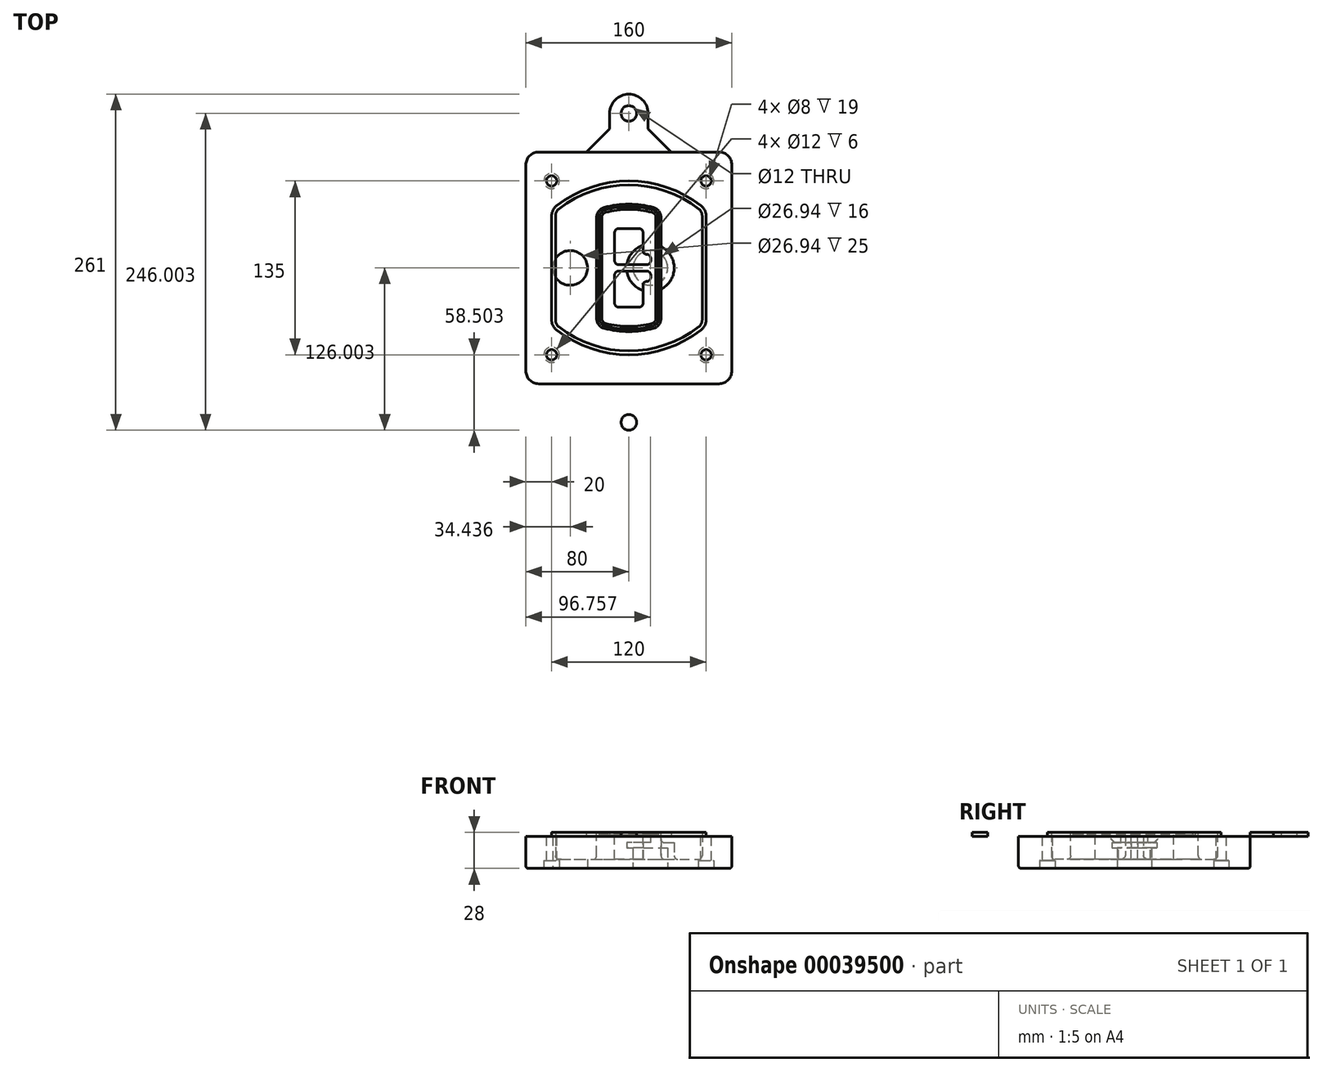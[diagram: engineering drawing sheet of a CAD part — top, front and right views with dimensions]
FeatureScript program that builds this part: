
annotation { "Feature Type Name" : "Feature", "Feature Type Description" : "" }
export const myFeature = defineFeature(function(context is Context, id is Id, definition is map)
    precondition{}
    {
        {
            var Q0;
            Q0=qCreatedBy(makeId("Top.planeOp"),FACE);
            var sketch = newSketch(context, id + "F0", { "sketchPlane" : qUnion([Q0])});
            skPoint(sketch, "E0.rect.middle", {"position": v(0, 0) * mm});
            skLineSegment(sketch, "E1.bottom", {"start": v(24.05, 28.38) * mm, "end": v(164.05, 28.38) * mm});
            skLineSegment(sketch, "E1.top", {"start": v(24.05, 208.38) * mm, "end": v(164.05, 208.38) * mm});
            skLineSegment(sketch, "E1.left", {"start": v(14.05, 38.38) * mm, "end": v(14.05, 198.38) * mm});
            skLineSegment(sketch, "E1.right", {"start": v(174.05, 38.38) * mm, "end": v(174.05, 198.38) * mm});
            skLineSegment(sketch, "E2", {"start": v(14.05, 208.38) * mm, "end": v(174.05, 28.38) * mm, "construction": true});
            skLineSegment(sketch, "E3", {"start": v(174.05, 208.38) * mm, "end": v(14.05, 28.38) * mm, "construction": true});
            skCircle(sketch, "E4", {"center": v(34.05, 185.88) * mm, "radius": 4 * mm});
            skCircle(sketch, "E5", {"center": v(154.05, 185.88) * mm, "radius": 4 * mm});
            skCircle(sketch, "E6", {"center": v(154.05, 50.88) * mm, "radius": 4 * mm});
            skCircle(sketch, "E7", {"center": v(34.05, 50.88) * mm, "radius": 4 * mm});
            skLineSegment(sketch, "E8", {"start": v(34.05, 185.88) * mm, "end": v(154.05, 185.88) * mm, "construction": true});
            skLineSegment(sketch, "E9", {"start": v(154.05, 185.88) * mm, "end": v(154.05, 50.88) * mm, "construction": true});
            skLineSegment(sketch, "E10", {"start": v(154.05, 50.88) * mm, "end": v(34.05, 50.88) * mm, "construction": true});
            skLineSegment(sketch, "E11", {"start": v(34.05, 50.88) * mm, "end": v(34.05, 185.88) * mm, "construction": true});
            skLineSegment(sketch, "E12", {"start": v(34.05, 158.68) * mm, "end": v(34.05, 78.09) * mm});
            skLineSegment(sketch, "E13", {"start": v(154.05, 158.68) * mm, "end": v(154.05, 78.09) * mm});
            skArc(sketch, "E14", {"start": v(150.2, 166.56) * mm, "mid": v(94.05, 185.88) * mm, "end": v(37.9, 166.56) * mm});
            skArc(sketch, "E15", {"start": v(37.9, 70.2) * mm, "mid": v(94.05, 50.88) * mm, "end": v(150.2, 70.2) * mm});
            skLineSegment(sketch, "E16", {"start": v(34.05, 118.38) * mm, "end": v(154.05, 118.38) * mm, "construction": true});
            skPoint(sketch, "E17.visualSharp", {"position": v(34.05, 73.38) * mm});
            skArc(sketch, "E17.filletArc", {"start": v(34.05, 78.09) * mm, "mid": v(35.06, 73.7) * mm, "end": v(37.9, 70.2) * mm});
            skPoint(sketch, "E18.visualSharp", {"position": v(34.05, 163.38) * mm});
            skArc(sketch, "E18.filletArc", {"start": v(37.9, 166.56) * mm, "mid": v(35.06, 163.06) * mm, "end": v(34.05, 158.68) * mm});
            skPoint(sketch, "E19.visualSharp", {"position": v(154.05, 163.38) * mm});
            skArc(sketch, "E19.filletArc", {"start": v(154.05, 158.68) * mm, "mid": v(153.04, 163.06) * mm, "end": v(150.2, 166.56) * mm});
            skPoint(sketch, "E20.visualSharp", {"position": v(154.05, 73.38) * mm});
            skArc(sketch, "E20.filletArc", {"start": v(150.2, 70.2) * mm, "mid": v(153.04, 73.7) * mm, "end": v(154.05, 78.09) * mm});
            skPoint(sketch, "E21.visualSharp", {"position": v(14.05, 208.38) * mm});
            skArc(sketch, "E21.filletArc", {"start": v(24.05, 208.38) * mm, "mid": v(16.98, 205.45) * mm, "end": v(14.05, 198.38) * mm});
            skPoint(sketch, "E22.visualSharp", {"position": v(174.05, 208.38) * mm});
            skArc(sketch, "E22.filletArc", {"start": v(174.05, 198.38) * mm, "mid": v(171.12, 205.45) * mm, "end": v(164.05, 208.38) * mm});
            skPoint(sketch, "E23.visualSharp", {"position": v(174.05, 28.38) * mm});
            skArc(sketch, "E23.filletArc", {"start": v(164.05, 28.38) * mm, "mid": v(171.12, 31.31) * mm, "end": v(174.05, 38.38) * mm});
            skPoint(sketch, "E24.visualSharp", {"position": v(14.05, 28.38) * mm});
            skArc(sketch, "E24.filletArc", {"start": v(14.05, 38.38) * mm, "mid": v(16.98, 31.31) * mm, "end": v(24.05, 28.38) * mm});
            skArc(sketch, "E25.0", {"start": v(151.05, 158.68) * mm, "mid": v(150.34, 161.75) * mm, "end": v(148.36, 164.2) * mm});
            skLineSegment(sketch, "E25.1", {"start": v(151.05, 158.68) * mm, "end": v(151.05, 78.09) * mm});
            skArc(sketch, "E25.2", {"start": v(148.36, 72.57) * mm, "mid": v(150.34, 75.02) * mm, "end": v(151.05, 78.09) * mm});
            skArc(sketch, "E25.3", {"start": v(39.74, 72.57) * mm, "mid": v(94.05, 53.88) * mm, "end": v(148.36, 72.57) * mm});
            skArc(sketch, "E25.4", {"start": v(37.05, 78.09) * mm, "mid": v(37.76, 75.02) * mm, "end": v(39.74, 72.57) * mm});
            skArc(sketch, "E25.5", {"start": v(148.36, 164.2) * mm, "mid": v(94.05, 182.88) * mm, "end": v(39.74, 164.2) * mm});
            skLineSegment(sketch, "E25.6", {"start": v(37.05, 158.68) * mm, "end": v(37.05, 78.09) * mm});
            skArc(sketch, "E25.7", {"start": v(39.74, 164.2) * mm, "mid": v(37.76, 161.75) * mm, "end": v(37.05, 158.68) * mm});
            skArc(sketch, "E26.0", {"start": v(35.43, 169.71) * mm, "mid": v(31.47, 164.82) * mm, "end": v(30.05, 158.68) * mm});
            skArc(sketch, "E26.1", {"start": v(152.67, 169.71) * mm, "mid": v(94.05, 189.88) * mm, "end": v(35.43, 169.71) * mm});
            skArc(sketch, "E26.2", {"start": v(158.05, 158.68) * mm, "mid": v(156.63, 164.82) * mm, "end": v(152.67, 169.71) * mm});
            skLineSegment(sketch, "E26.3", {"start": v(158.05, 158.68) * mm, "end": v(158.05, 78.09) * mm});
            skArc(sketch, "E26.4", {"start": v(152.67, 67.05) * mm, "mid": v(156.63, 71.95) * mm, "end": v(158.05, 78.09) * mm});
            skLineSegment(sketch, "E26.5", {"start": v(30.05, 158.68) * mm, "end": v(30.05, 78.09) * mm});
            skArc(sketch, "E26.6", {"start": v(35.43, 67.05) * mm, "mid": v(94.05, 46.88) * mm, "end": v(152.67, 67.05) * mm});
            skArc(sketch, "E26.7", {"start": v(30.05, 78.09) * mm, "mid": v(31.47, 71.95) * mm, "end": v(35.43, 67.05) * mm});
            skSolve(sketch);
        }
        {
            var Q0;
            Q0=makeQuery(id+"F0.imprint","IMPRINT",FACE,{"disambiguationData":[TD([[makeQuery(id+"F0.imprint","IMPRINT",EDGE,{"derivedFrom":sQuery(id+"F0.wireOp",EDGE,"E1.bottom")}),1.0]])]});
            var Q1;
            Q1=makeQuery(id+"F0.imprint","IMPRINT",FACE,{"disambiguationData":[TD([[makeQuery(id+"F0.imprint","IMPRINT",EDGE,{"derivedFrom":sQuery(id+"F0.wireOp",EDGE,"E12")}),1.0]])]});
            var Q2;
            Q2=makeQuery(id+"F0.imprint","IMPRINT",FACE,{"disambiguationData":[TD([[makeQuery(id+"F0.imprint","IMPRINT",EDGE,{"derivedFrom":sQuery(id+"F0.wireOp",EDGE,"E25.0")}),1.0]])]});
            var Q3;
            Q3=makeQuery(id+"F0.imprint","IMPRINT",FACE,{"disambiguationData":[TD([[makeQuery(id+"F0.imprint","IMPRINT",EDGE,{"derivedFrom":sQuery(id+"F0.wireOp",EDGE,"E12")}),-1.0]])]});
            extrude(context, id + "F1", {"entities" : qUnion([Q0, Q1, Q2, Q3]), "oppositeDirection" : true, "depth" : 25 * mm});
        }
        {
            var Q0;
            Q0=makeQuery(id+"F0.imprint","IMPRINT",FACE,{"disambiguationData":[TD([[makeQuery(id+"F0.imprint","IMPRINT",EDGE,{"derivedFrom":sQuery(id+"F0.wireOp",EDGE,"E12")}),1.0]])]});
            extrude(context, id + "F2", {"entities" : qUnion([Q0]), "operationType" : NewBodyOperationType.ADD, "depth" : 3 * mm});
        }
        {
            var Q0;
            Q0=makeQuery(id+"F0.imprint","IMPRINT",FACE,{"disambiguationData":[TD([[makeQuery(id+"F0.imprint","IMPRINT",EDGE,{"derivedFrom":sQuery(id+"F0.wireOp",EDGE,"E25.0")}),1.0]])]});
            extrude(context, id + "F3", {"entities" : qUnion([Q0]), "operationType" : NewBodyOperationType.REMOVE, "oppositeDirection" : true, "depth" : 18 * mm});
        }
        {
            var Q0;
            Q0=makeQuery(id+"F2.opExtrude","CAP_FACE",FACE,{"disambiguationData":[OSD([sQuery(id+"F0.wireOp",EDGE,"E12"),sQuery(id+"F0.wireOp",EDGE,"E13"),sQuery(id+"F0.wireOp",EDGE,"E14"),sQuery(id+"F0.wireOp",EDGE,"E15"),sQuery(id+"F0.wireOp",EDGE,"E17.filletArc"),sQuery(id+"F0.wireOp",EDGE,"E18.filletArc"),sQuery(id+"F0.wireOp",EDGE,"E19.filletArc"),sQuery(id+"F0.wireOp",EDGE,"E20.filletArc"),sQuery(id+"F0.wireOp",EDGE,"E25.0"),sQuery(id+"F0.wireOp",EDGE,"E25.1"),sQuery(id+"F0.wireOp",EDGE,"E25.2"),sQuery(id+"F0.wireOp",EDGE,"E25.3"),sQuery(id+"F0.wireOp",EDGE,"E25.4"),sQuery(id+"F0.wireOp",EDGE,"E25.5"),sQuery(id+"F0.wireOp",EDGE,"E25.6"),sQuery(id+"F0.wireOp",EDGE,"E25.7")])],"isStart":false});
            var sketch = newSketch(context, id + "F4", { "sketchPlane" : qUnion([Q0])});
            skArc(sketch, "E27.0", {"start": v(74.97, 71.41) * mm, "mid": v(94.05, 68.88) * mm, "end": v(113.13, 71.41) * mm});
            skArc(sketch, "E28.0", {"start": v(113.13, 165.35) * mm, "mid": v(94.05, 167.88) * mm, "end": v(74.97, 165.35) * mm});
            skLineSegment(sketch, "E29", {"start": v(69.05, 157.63) * mm, "end": v(69.05, 79.14) * mm});
            skLineSegment(sketch, "E30", {"start": v(119.05, 157.63) * mm, "end": v(119.05, 79.14) * mm});
            skLineSegment(sketch, "E31", {"start": v(69.05, 163.48) * mm, "end": v(119.05, 163.48) * mm, "construction": true});
            skLineSegment(sketch, "E32", {"start": v(69.05, 73.28) * mm, "end": v(119.05, 73.28) * mm, "construction": true});
            skPoint(sketch, "E33.visualSharp", {"position": v(69.05, 163.48) * mm});
            skArc(sketch, "E33.filletArc", {"start": v(74.97, 165.35) * mm, "mid": v(70.7, 162.5) * mm, "end": v(69.05, 157.63) * mm});
            skPoint(sketch, "E34.visualSharp", {"position": v(119.05, 163.48) * mm});
            skArc(sketch, "E34.filletArc", {"start": v(119.05, 157.63) * mm, "mid": v(117.4, 162.5) * mm, "end": v(113.13, 165.35) * mm});
            skPoint(sketch, "E35.visualSharp", {"position": v(119.05, 73.28) * mm});
            skArc(sketch, "E35.filletArc", {"start": v(113.13, 71.41) * mm, "mid": v(117.4, 74.27) * mm, "end": v(119.05, 79.14) * mm});
            skPoint(sketch, "E36.visualSharp", {"position": v(69.05, 73.28) * mm});
            skArc(sketch, "E36.filletArc", {"start": v(69.05, 79.14) * mm, "mid": v(70.7, 74.27) * mm, "end": v(74.97, 71.41) * mm});
            skArc(sketch, "E37.0", {"start": v(148.36, 164.2) * mm, "mid": v(94.05, 182.88) * mm, "end": v(39.74, 164.2) * mm});
            skArc(sketch, "E37.1", {"start": v(39.74, 164.2) * mm, "mid": v(37.76, 161.75) * mm, "end": v(37.05, 158.68) * mm});
            skLineSegment(sketch, "E37.2", {"start": v(37.05, 158.68) * mm, "end": v(37.05, 78.09) * mm});
            skArc(sketch, "E37.3", {"start": v(37.05, 78.09) * mm, "mid": v(37.76, 75.02) * mm, "end": v(39.74, 72.57) * mm});
            skArc(sketch, "E37.4", {"start": v(39.74, 72.57) * mm, "mid": v(94.05, 53.88) * mm, "end": v(148.36, 72.57) * mm});
            skArc(sketch, "E37.5", {"start": v(148.36, 72.57) * mm, "mid": v(150.34, 75.02) * mm, "end": v(151.05, 78.09) * mm});
            skLineSegment(sketch, "E37.6", {"start": v(151.05, 158.68) * mm, "end": v(151.05, 78.09) * mm});
            skArc(sketch, "E37.7", {"start": v(151.05, 158.68) * mm, "mid": v(150.34, 161.75) * mm, "end": v(148.36, 164.2) * mm});
            skLineSegment(sketch, "E38.0", {"start": v(117.05, 157.63) * mm, "end": v(117.05, 79.14) * mm});
            skArc(sketch, "E38.1", {"start": v(112.61, 73.34) * mm, "mid": v(115.81, 75.49) * mm, "end": v(117.05, 79.14) * mm});
            skArc(sketch, "E38.2", {"start": v(75.49, 73.34) * mm, "mid": v(94.05, 70.88) * mm, "end": v(112.61, 73.34) * mm});
            skArc(sketch, "E38.3", {"start": v(71.05, 79.14) * mm, "mid": v(72.29, 75.49) * mm, "end": v(75.49, 73.34) * mm});
            skLineSegment(sketch, "E38.4", {"start": v(71.05, 157.63) * mm, "end": v(71.05, 79.14) * mm});
            skArc(sketch, "E38.5", {"start": v(117.05, 157.63) * mm, "mid": v(115.81, 161.28) * mm, "end": v(112.61, 163.42) * mm});
            skArc(sketch, "E38.6", {"start": v(75.49, 163.42) * mm, "mid": v(72.29, 161.28) * mm, "end": v(71.05, 157.63) * mm});
            skArc(sketch, "E38.7", {"start": v(112.61, 163.42) * mm, "mid": v(94.05, 165.88) * mm, "end": v(75.49, 163.42) * mm});
            skArc(sketch, "E39.0", {"start": v(115.05, 157.63) * mm, "mid": v(114.23, 160.06) * mm, "end": v(112.1, 161.5) * mm});
            skLineSegment(sketch, "E39.1", {"start": v(115.05, 157.63) * mm, "end": v(115.05, 79.14) * mm});
            skArc(sketch, "E39.2", {"start": v(112.1, 75.27) * mm, "mid": v(114.23, 76.7) * mm, "end": v(115.05, 79.14) * mm});
            skArc(sketch, "E39.3", {"start": v(76, 75.27) * mm, "mid": v(94.05, 72.88) * mm, "end": v(112.1, 75.27) * mm});
            skArc(sketch, "E39.4", {"start": v(73.05, 79.14) * mm, "mid": v(73.87, 76.7) * mm, "end": v(76, 75.27) * mm});
            skArc(sketch, "E39.5", {"start": v(112.1, 161.5) * mm, "mid": v(94.05, 163.88) * mm, "end": v(76, 161.5) * mm});
            skLineSegment(sketch, "E39.6", {"start": v(73.05, 157.63) * mm, "end": v(73.05, 79.14) * mm});
            skArc(sketch, "E39.7", {"start": v(76, 161.5) * mm, "mid": v(73.87, 160.06) * mm, "end": v(73.05, 157.63) * mm});
            skLineSegment(sketch, "E40", {"start": v(69.05, 118.38) * mm, "end": v(119.05, 118.38) * mm, "construction": true});
            skLineSegment(sketch, "E41", {"start": v(83.05, 123.88) * mm, "end": v(83.05, 145.88) * mm});
            skLineSegment(sketch, "E42", {"start": v(86.05, 148.88) * mm, "end": v(102.05, 148.88) * mm});
            skLineSegment(sketch, "E43", {"start": v(105.05, 145.88) * mm, "end": v(105.05, 131.88) * mm});
            skLineSegment(sketch, "E44", {"start": v(108.05, 128.88) * mm, "end": v(108.05, 128.88) * mm});
            skLineSegment(sketch, "E45", {"start": v(111.05, 125.88) * mm, "end": v(111.05, 123.88) * mm});
            skLineSegment(sketch, "E46", {"start": v(108.05, 120.88) * mm, "end": v(86.05, 120.88) * mm});
            skPoint(sketch, "E47.visualSharp", {"position": v(83.05, 148.88) * mm});
            skArc(sketch, "E47.filletArc", {"start": v(86.05, 148.88) * mm, "mid": v(83.93, 148) * mm, "end": v(83.05, 145.88) * mm});
            skPoint(sketch, "E48.visualSharp", {"position": v(105.05, 148.88) * mm});
            skArc(sketch, "E48.filletArc", {"start": v(105.05, 145.88) * mm, "mid": v(104.17, 148) * mm, "end": v(102.05, 148.88) * mm});
            skPoint(sketch, "E49.visualSharp", {"position": v(105.05, 128.88) * mm});
            skArc(sketch, "E49.filletArc", {"start": v(105.05, 131.88) * mm, "mid": v(105.93, 129.76) * mm, "end": v(108.05, 128.88) * mm});
            skPoint(sketch, "E50.visualSharp", {"position": v(111.05, 128.88) * mm});
            skArc(sketch, "E50.filletArc", {"start": v(111.05, 125.88) * mm, "mid": v(110.17, 128) * mm, "end": v(108.05, 128.88) * mm});
            skPoint(sketch, "E51.visualSharp", {"position": v(111.05, 120.88) * mm});
            skArc(sketch, "E51.filletArc", {"start": v(108.05, 120.88) * mm, "mid": v(110.17, 121.76) * mm, "end": v(111.05, 123.88) * mm});
            skPoint(sketch, "E52.visualSharp", {"position": v(83.05, 120.88) * mm});
            skArc(sketch, "E52.filletArc", {"start": v(83.05, 123.88) * mm, "mid": v(83.93, 121.76) * mm, "end": v(86.05, 120.88) * mm});
            skLineSegment(sketch, "E53.0.MirrorCS", {"start": v(108.05, 115.88) * mm, "end": v(86.05, 115.88) * mm});
            skArc(sketch, "E54.0.MirrorCS", {"start": v(83.05, 112.88) * mm, "mid": v(83.93, 115) * mm, "end": v(86.05, 115.88) * mm});
            skLineSegment(sketch, "E55.0.MirrorCS", {"start": v(83.05, 112.88) * mm, "end": v(83.05, 90.88) * mm});
            skArc(sketch, "E56.0.MirrorCS", {"start": v(86.05, 87.88) * mm, "mid": v(83.93, 88.76) * mm, "end": v(83.05, 90.88) * mm});
            skLineSegment(sketch, "E57.0.MirrorCS", {"start": v(86.05, 87.88) * mm, "end": v(102.05, 87.88) * mm});
            skArc(sketch, "E58.0.MirrorCS", {"start": v(105.05, 90.88) * mm, "mid": v(104.17, 88.76) * mm, "end": v(102.05, 87.88) * mm});
            skLineSegment(sketch, "E59.0.MirrorCS", {"start": v(105.05, 90.88) * mm, "end": v(105.05, 104.88) * mm});
            skArc(sketch, "E60.0.MirrorCS", {"start": v(105.05, 104.88) * mm, "mid": v(105.93, 107) * mm, "end": v(108.05, 107.88) * mm});
            skArc(sketch, "E61.0.MirrorCS", {"start": v(111.05, 110.88) * mm, "mid": v(110.17, 108.76) * mm, "end": v(108.05, 107.88) * mm});
            skLineSegment(sketch, "E62.0.MirrorCS", {"start": v(111.05, 110.88) * mm, "end": v(111.05, 112.88) * mm});
            skArc(sketch, "E63.0.MirrorCS", {"start": v(108.05, 115.88) * mm, "mid": v(110.17, 115) * mm, "end": v(111.05, 112.88) * mm});
            skSolve(sketch);
        }
        {
            var Q0;
            Q0=makeQuery(id+"F4.imprint","IMPRINT",FACE,{"disambiguationData":[TD([[makeQuery(id+"F4.imprint","IMPRINT",EDGE,{"derivedFrom":sQuery(id+"F4.wireOp",EDGE,"E27.0")}),1.0]])]});
            var Q1;
            Q1=makeQuery(id+"F4.imprint","IMPRINT",FACE,{"disambiguationData":[TD([[makeQuery(id+"F4.imprint","IMPRINT",EDGE,{"derivedFrom":sQuery(id+"F4.wireOp",EDGE,"E38.0")}),-1.0]])]});
            var Q2;
            Q2=makeQuery(id+"F4.imprint","IMPRINT",FACE,{"disambiguationData":[TD([[makeQuery(id+"F4.imprint","IMPRINT",EDGE,{"derivedFrom":sQuery(id+"F4.wireOp",EDGE,"E39.0")}),1.0]])]});
            extrude(context, id + "F5", {"entities" : qUnion([Q0, Q1, Q2]), "operationType" : NewBodyOperationType.ADD, "endBound" : BoundingType.UP_TO_NEXT, "oppositeDirection" : true, "depth" : 25 * mm});
        }
        {
            var Q0;
            Q0=makeQuery(id+"F4.imprint","IMPRINT",FACE,{"disambiguationData":[TD([[makeQuery(id+"F4.imprint","IMPRINT",EDGE,{"derivedFrom":sQuery(id+"F4.wireOp",EDGE,"E38.0")}),-1.0]])]});
            extrude(context, id + "F6", {"entities" : qUnion([Q0]), "operationType" : NewBodyOperationType.REMOVE, "oppositeDirection" : true, "depth" : 2 * mm});
        }
        {
            var Q0;
            Q0=makeQuery(id+"F1.opExtrude","CAP_FACE",FACE,{"disambiguationData":[OSD([sQuery(id+"F0.wireOp",EDGE,"E1.bottom"),sQuery(id+"F0.wireOp",EDGE,"E1.top"),sQuery(id+"F0.wireOp",EDGE,"E1.left"),sQuery(id+"F0.wireOp",EDGE,"E1.right"),sQuery(id+"F0.wireOp",EDGE,"E4"),sQuery(id+"F0.wireOp",EDGE,"E5"),sQuery(id+"F0.wireOp",EDGE,"E6"),sQuery(id+"F0.wireOp",EDGE,"E7"),sQuery(id+"F0.wireOp",EDGE,"E21.filletArc"),sQuery(id+"F0.wireOp",EDGE,"E22.filletArc"),sQuery(id+"F0.wireOp",EDGE,"E23.filletArc"),sQuery(id+"F0.wireOp",EDGE,"E24.filletArc")])],"isStart":false});
            var sketch = newSketch(context, id + "F7", { "sketchPlane" : qUnion([Q0])});
            skCircle(sketch, "E64", {"center": v(110.8, -118.38) * mm, "radius": 13.47 * mm});
            skCircle(sketch, "E65", {"center": v(48.49, -118.38) * mm, "radius": 13.47 * mm});
            skLineSegment(sketch, "E66", {"start": v(174.05, -118.38) * mm, "end": v(14.05, -118.38) * mm});
            skCircle(sketch, "E67", {"center": v(110.8, -118.38) * mm, "radius": 18.47 * mm});
            skCircle(sketch, "E68", {"center": v(154.05, -185.88) * mm, "radius": 6 * mm});
            skCircle(sketch, "E69", {"center": v(34.05, -185.88) * mm, "radius": 6 * mm});
            skCircle(sketch, "E70", {"center": v(34.05, -50.88) * mm, "radius": 6 * mm});
            skCircle(sketch, "E71", {"center": v(154.05, -50.88) * mm, "radius": 6 * mm});
            skSolve(sketch);
        }
        {
            var Q0;
            {var subQ1=sQuery(id+"F7.wireOp",EDGE,"E66");var subQ4=sQuery(id+"F7.wireOp",EDGE,"E64");var subQ6=makeQuery(id+"F7.imprint","INTERSECT",VERTEX,{"disambiguationData":[OD(0.0)],"derivedFrom":[subQ4,subQ1]});Q0=makeQuery(id+"F7.imprint","IMPRINT",FACE,{"disambiguationData":[TD([[makeQuery(id+"F7.imprint","IMPRINT",EDGE,{"disambiguationData":[TD([[subQ6,-1.0]])],"derivedFrom":subQ4}),-1.0]])]});}
            var Q1;
            {var subQ0=sQuery(id+"F7.wireOp",EDGE,"E66");var subQ1=sQuery(id+"F7.wireOp",EDGE,"E64");var subQ3=makeQuery(id+"F7.imprint","INTERSECT",VERTEX,{"disambiguationData":[OD(0.0)],"derivedFrom":[subQ1,subQ0]});Q1=makeQuery(id+"F7.imprint","IMPRINT",FACE,{"disambiguationData":[TD([[makeQuery(id+"F7.imprint","IMPRINT",EDGE,{"disambiguationData":[TD([[subQ3,-1.0]])],"derivedFrom":subQ1}),1.0]])]});}
            var Q2;
            {var subQ0=sQuery(id+"F7.wireOp",EDGE,"E66");var subQ1=sQuery(id+"F7.wireOp",EDGE,"E64");var subQ3=makeQuery(id+"F7.imprint","INTERSECT",VERTEX,{"disambiguationData":[OD(0.0)],"derivedFrom":[subQ1,subQ0]});Q2=makeQuery(id+"F7.imprint","IMPRINT",FACE,{"disambiguationData":[TD([[makeQuery(id+"F7.imprint","IMPRINT",EDGE,{"disambiguationData":[TD([[subQ3,1.0]])],"derivedFrom":subQ1}),1.0]])]});}
            var Q3;
            {var subQ1=sQuery(id+"F7.wireOp",EDGE,"E66");var subQ4=sQuery(id+"F7.wireOp",EDGE,"E64");var subQ6=makeQuery(id+"F7.imprint","INTERSECT",VERTEX,{"disambiguationData":[OD(0.0)],"derivedFrom":[subQ4,subQ1]});Q3=makeQuery(id+"F7.imprint","IMPRINT",FACE,{"disambiguationData":[TD([[makeQuery(id+"F7.imprint","IMPRINT",EDGE,{"disambiguationData":[TD([[subQ6,1.0]])],"derivedFrom":subQ4}),-1.0]])]});}
            extrude(context, id + "F8", {"entities" : qUnion([Q0, Q1, Q2, Q3]), "operationType" : NewBodyOperationType.ADD, "oppositeDirection" : true, "depth" : 20 * mm});
        }
        {
            var Q0;
            {var subQ0=sQuery(id+"F7.wireOp",EDGE,"E66");var subQ1=sQuery(id+"F7.wireOp",EDGE,"E64");var subQ3=makeQuery(id+"F7.imprint","INTERSECT",VERTEX,{"disambiguationData":[OD(0.0)],"derivedFrom":[subQ1,subQ0]});Q0=makeQuery(id+"F7.imprint","IMPRINT",FACE,{"disambiguationData":[TD([[makeQuery(id+"F7.imprint","IMPRINT",EDGE,{"disambiguationData":[TD([[subQ3,-1.0]])],"derivedFrom":subQ1}),1.0]])]});}
            var Q1;
            {var subQ0=sQuery(id+"F7.wireOp",EDGE,"E66");var subQ1=sQuery(id+"F7.wireOp",EDGE,"E64");var subQ3=makeQuery(id+"F7.imprint","INTERSECT",VERTEX,{"disambiguationData":[OD(0.0)],"derivedFrom":[subQ1,subQ0]});Q1=makeQuery(id+"F7.imprint","IMPRINT",FACE,{"disambiguationData":[TD([[makeQuery(id+"F7.imprint","IMPRINT",EDGE,{"disambiguationData":[TD([[subQ3,1.0]])],"derivedFrom":subQ1}),1.0]])]});}
            extrude(context, id + "F9", {"entities" : qUnion([Q0, Q1]), "operationType" : NewBodyOperationType.REMOVE, "oppositeDirection" : true, "depth" : 16 * mm});
        }
        {
            var Q0;
            {var subQ0=sQuery(id+"F7.wireOp",EDGE,"E66");var subQ1=sQuery(id+"F7.wireOp",EDGE,"E65");var subQ3=makeQuery(id+"F7.imprint","INTERSECT",VERTEX,{"disambiguationData":[OD(0.0)],"derivedFrom":[subQ1,subQ0]});Q0=makeQuery(id+"F7.imprint","IMPRINT",FACE,{"disambiguationData":[TD([[makeQuery(id+"F7.imprint","IMPRINT",EDGE,{"disambiguationData":[TD([[subQ3,-1.0]])],"derivedFrom":subQ1}),1.0]])]});}
            var Q1;
            {var subQ0=sQuery(id+"F7.wireOp",EDGE,"E66");var subQ1=sQuery(id+"F7.wireOp",EDGE,"E65");var subQ3=makeQuery(id+"F7.imprint","INTERSECT",VERTEX,{"disambiguationData":[OD(0.0)],"derivedFrom":[subQ1,subQ0]});Q1=makeQuery(id+"F7.imprint","IMPRINT",FACE,{"disambiguationData":[TD([[makeQuery(id+"F7.imprint","IMPRINT",EDGE,{"disambiguationData":[TD([[subQ3,1.0]])],"derivedFrom":subQ1}),1.0]])]});}
            extrude(context, id + "F10", {"entities" : qUnion([Q0, Q1]), "operationType" : NewBodyOperationType.REMOVE, "oppositeDirection" : true, "depth" : 25 * mm});
        }
        {
            var Q0;
            Q0=makeQuery(id+"F7.imprint","IMPRINT",FACE,{"disambiguationData":[TD([[makeQuery(id+"F7.imprint","IMPRINT",EDGE,{"derivedFrom":sQuery(id+"F7.wireOp",EDGE,"E68")}),1.0]])]});
            var Q1;
            Q1=makeQuery(id+"F7.imprint","IMPRINT",FACE,{"disambiguationData":[TD([[makeQuery(id+"F7.imprint","IMPRINT",EDGE,{"derivedFrom":makeQuery(id+"F1.opExtrude","CAP_EDGE",EDGE,{"disambiguationData":[OSD([sQuery(id+"F0.wireOp",EDGE,"E5")])],"isStart":false})}),-1.0]])]});
            var Q2;
            Q2=makeQuery(id+"F7.imprint","IMPRINT",FACE,{"disambiguationData":[TD([[makeQuery(id+"F7.imprint","IMPRINT",EDGE,{"derivedFrom":sQuery(id+"F7.wireOp",EDGE,"E69")}),1.0]])]});
            var Q3;
            Q3=makeQuery(id+"F7.imprint","IMPRINT",FACE,{"disambiguationData":[TD([[makeQuery(id+"F7.imprint","IMPRINT",EDGE,{"derivedFrom":makeQuery(id+"F1.opExtrude","CAP_EDGE",EDGE,{"disambiguationData":[OSD([sQuery(id+"F0.wireOp",EDGE,"E4")])],"isStart":false})}),-1.0]])]});
            var Q4;
            Q4=makeQuery(id+"F7.imprint","IMPRINT",FACE,{"disambiguationData":[TD([[makeQuery(id+"F7.imprint","IMPRINT",EDGE,{"derivedFrom":sQuery(id+"F7.wireOp",EDGE,"E70")}),1.0]])]});
            var Q5;
            Q5=makeQuery(id+"F7.imprint","IMPRINT",FACE,{"disambiguationData":[TD([[makeQuery(id+"F7.imprint","IMPRINT",EDGE,{"derivedFrom":makeQuery(id+"F1.opExtrude","CAP_EDGE",EDGE,{"disambiguationData":[OSD([sQuery(id+"F0.wireOp",EDGE,"E7")])],"isStart":false})}),-1.0]])]});
            var Q6;
            Q6=makeQuery(id+"F7.imprint","IMPRINT",FACE,{"disambiguationData":[TD([[makeQuery(id+"F7.imprint","IMPRINT",EDGE,{"derivedFrom":sQuery(id+"F7.wireOp",EDGE,"E71")}),1.0]])]});
            var Q7;
            Q7=makeQuery(id+"F7.imprint","IMPRINT",FACE,{"disambiguationData":[TD([[makeQuery(id+"F7.imprint","IMPRINT",EDGE,{"derivedFrom":makeQuery(id+"F1.opExtrude","CAP_EDGE",EDGE,{"disambiguationData":[OSD([sQuery(id+"F0.wireOp",EDGE,"E6")])],"isStart":false})}),-1.0]])]});
            extrude(context, id + "F11", {"entities" : qUnion([Q0, Q1, Q2, Q3, Q4, Q5, Q6, Q7]), "operationType" : NewBodyOperationType.REMOVE, "oppositeDirection" : true, "depth" : 6 * mm});
        }
        {
            var Q0;
            Q0=makeQuery(id+"F9.boolean.opBoolean","COPY",FACE,{"derivedFrom":makeQuery(id+"F9.opExtrude","CAP_FACE",FACE,{"disambiguationData":[OSD([sQuery(id+"F7.wireOp",EDGE,"E64")])],"isStart":false})});
            var sketch = newSketch(context, id + "F12", { "sketchPlane" : qUnion([Q0])});
            skArc(sketch, "E72.0", {"start": v(105.05, -100.83) * mm, "mid": v(96.62, -106.56) * mm, "end": v(92.5, -115.88) * mm});
            skArc(sketch, "E72.1", {"start": v(92.5, -120.88) * mm, "mid": v(96.62, -130.2) * mm, "end": v(105.05, -135.93) * mm});
            skLineSegment(sketch, "E73", {"start": v(92.5, -120.88) * mm, "end": v(108.05, -120.88) * mm});
            skLineSegment(sketch, "E74.0", {"start": v(108.05, -115.88) * mm, "end": v(92.5, -115.88) * mm});
            skArc(sketch, "E74.1", {"start": v(108.05, -115.88) * mm, "mid": v(110.17, -115) * mm, "end": v(111.05, -112.88) * mm});
            skLineSegment(sketch, "E74.2", {"start": v(111.05, -110.88) * mm, "end": v(111.05, -112.88) * mm});
            skArc(sketch, "E74.3", {"start": v(111.05, -110.88) * mm, "mid": v(110.17, -108.76) * mm, "end": v(108.05, -107.88) * mm});
            skArc(sketch, "E74.4", {"start": v(105.05, -104.88) * mm, "mid": v(105.93, -107) * mm, "end": v(108.05, -107.88) * mm});
            skLineSegment(sketch, "E74.5", {"start": v(105.05, -100.83) * mm, "end": v(105.05, -104.88) * mm});
            skLineSegment(sketch, "E74.7", {"start": v(108.05, -120.88) * mm, "end": v(92.5, -120.88) * mm});
            skArc(sketch, "E74.8", {"start": v(108.05, -120.88) * mm, "mid": v(110.17, -121.76) * mm, "end": v(111.05, -123.88) * mm});
            skLineSegment(sketch, "E74.9", {"start": v(111.05, -125.88) * mm, "end": v(111.05, -123.88) * mm});
            skArc(sketch, "E74.10", {"start": v(111.05, -125.88) * mm, "mid": v(110.17, -128) * mm, "end": v(108.05, -128.88) * mm});
            skArc(sketch, "E74.11", {"start": v(105.05, -131.88) * mm, "mid": v(105.93, -129.76) * mm, "end": v(108.05, -128.88) * mm});
            skLineSegment(sketch, "E74.12", {"start": v(105.05, -135.93) * mm, "end": v(105.05, -131.88) * mm});
            skPoint(sketch, "E75.orphan", {"position": v(105.05, -145.88) * mm});
            skPoint(sketch, "E76.orphan", {"position": v(86.05, -120.88) * mm});
            skPoint(sketch, "E77.orphan", {"position": v(86.05, -115.88) * mm});
            skPoint(sketch, "E78.orphan", {"position": v(105.05, -90.88) * mm});
            skSolve(sketch);
        }
        {
            var Q0;
            {var subQ7=sQuery(id+"F12.wireOp",EDGE,"E72.0");var subQ14=sQuery(id+"F12.wireOp",EDGE,"E72.1");var subQ16=sQuery(id+"F12.wireOp",EDGE,"E74.1");var subQ18=sQuery(id+"F12.wireOp",EDGE,"E74.8");Q0=qUnion([makeQuery(id+"F12.imprint","IMPRINT",FACE,{"disambiguationData":[TD([[makeQuery(id+"F12.imprint","IMPRINT",EDGE,{"derivedFrom":subQ7}),1.0]])]}),makeQuery(id+"F12.imprint","IMPRINT",FACE,{"disambiguationData":[TD([[makeQuery(id+"F12.imprint","IMPRINT",EDGE,{"derivedFrom":subQ14}),1.0]])]}),makeQuery(id+"F12.imprint","IMPRINT",FACE,{"disambiguationData":[TD([[makeQuery(id+"F12.imprint","IMPRINT",EDGE,{"derivedFrom":subQ16}),1.0]])]}),makeQuery(id+"F12.imprint","IMPRINT",FACE,{"disambiguationData":[TD([[makeQuery(id+"F12.imprint","IMPRINT",EDGE,{"derivedFrom":subQ18}),-1.0]])]})]);}
            var Q1;
            Q1=makeQuery(id+"F5.boolean.opBoolean","SPLIT",FACE,{"disambiguationData":[TD([makeQuery(id+"F5.opExtrude","SWEPT_FACE",FACE,{"disambiguationData":[OSD([sQuery(id+"F4.wireOp",EDGE,"E41")])]})])],"derivedFrom":makeQuery(id+"F3.boolean.opBoolean","COPY",FACE,{"derivedFrom":makeQuery(id+"F3.opExtrude","CAP_FACE",FACE,{"disambiguationData":[OSD([sQuery(id+"F0.wireOp",EDGE,"E25.0"),sQuery(id+"F0.wireOp",EDGE,"E25.1"),sQuery(id+"F0.wireOp",EDGE,"E25.2"),sQuery(id+"F0.wireOp",EDGE,"E25.3"),sQuery(id+"F0.wireOp",EDGE,"E25.4"),sQuery(id+"F0.wireOp",EDGE,"E25.5"),sQuery(id+"F0.wireOp",EDGE,"E25.6"),sQuery(id+"F0.wireOp",EDGE,"E25.7")])],"isStart":false})})});
            extrude(context, id + "F13", {"entities" : qUnion([Q0]), "operationType" : NewBodyOperationType.REMOVE, "endBound" : BoundingType.UP_TO_SURFACE, "endBoundEntityFace" : qUnion([Q1]), "depth" : 25 * mm});
        }
        {
            var Q0;
            Q0=makeQuery(id+"F3.boolean.opBoolean","COPY",EDGE,{"derivedFrom":makeQuery(id+"F3.opExtrude","CAP_EDGE",EDGE,{"disambiguationData":[OSD([sQuery(id+"F0.wireOp",EDGE,"E25.6")])],"isStart":false})});
            var Q1;
            Q1=makeQuery(id+"F8.boolean.opBoolean","INTERSECT",EDGE,{"derivedFrom":[makeQuery(id+"F5.opExtrude","SWEPT_FACE",FACE,{"disambiguationData":[OSD([sQuery(id+"F4.wireOp",EDGE,"E30")])]}),makeQuery(id+"F8.opExtrude","CAP_FACE",FACE,{"disambiguationData":[OSD([sQuery(id+"F7.wireOp",EDGE,"E67")])],"isStart":false})]});
            var Q2;
            Q2=makeQuery(id+"F8.boolean.opBoolean","INTERSECT",EDGE,{"disambiguationData":[OD(1.0)],"derivedFrom":[makeQuery(id+"F5.opExtrude","SWEPT_FACE",FACE,{"disambiguationData":[OSD([sQuery(id+"F4.wireOp",EDGE,"E30")])]}),makeQuery(id+"F8.opExtrude","SWEPT_FACE",FACE,{"disambiguationData":[OSD([sQuery(id+"F7.wireOp",EDGE,"E67")])]})]});
            var Q3;
            {var subQ0=sQuery(id+"F4.wireOp",EDGE,"E30");Q3=makeQuery(id+"F8.boolean.opBoolean","SPLIT",EDGE,{"disambiguationData":[TD([makeQuery(id+"F5.opExtrude","SWEPT_FACE",FACE,{"disambiguationData":[OSD([sQuery(id+"F4.wireOp",EDGE,"E35.filletArc")])]})])],"derivedFrom":makeQuery(id+"F5.opExtrude","CAP_EDGE",EDGE,{"disambiguationData":[OSD([subQ0])],"isStart":false})});}
            var Q4;
            {var subQ0=sQuery(id+"F0.wireOp",EDGE,"E25.7");var subQ1=sQuery(id+"F0.wireOp",EDGE,"E25.1");var subQ2=sQuery(id+"F0.wireOp",EDGE,"E25.6");var subQ3=sQuery(id+"F0.wireOp",EDGE,"E25.5");var subQ4=sQuery(id+"F0.wireOp",EDGE,"E25.4");var subQ5=sQuery(id+"F0.wireOp",EDGE,"E25.0");var subQ6=sQuery(id+"F0.wireOp",EDGE,"E25.2");var subQ7=sQuery(id+"F0.wireOp",EDGE,"E25.3");Q4=makeQuery(id+"F8.boolean.opBoolean","INTERSECT",EDGE,{"derivedFrom":[makeQuery(id+"F5.boolean.opBoolean","SPLIT",FACE,{"disambiguationData":[TD([makeQuery(id+"F2.opExtrude","SWEPT_FACE",FACE,{"disambiguationData":[OSD([subQ5])]})])],"derivedFrom":makeQuery(id+"F3.boolean.opBoolean","COPY",FACE,{"derivedFrom":makeQuery(id+"F3.opExtrude","CAP_FACE",FACE,{"disambiguationData":[OSD([subQ5,subQ1,subQ6,subQ7,subQ4,subQ3,subQ2,subQ0])],"isStart":false})})}),makeQuery(id+"F8.opExtrude","SWEPT_FACE",FACE,{"disambiguationData":[OSD([sQuery(id+"F7.wireOp",EDGE,"E67")])]})]});}
            var Q5;
            Q5=makeQuery(id+"F8.boolean.opBoolean","INTERSECT",EDGE,{"disambiguationData":[OD(0.0)],"derivedFrom":[makeQuery(id+"F5.opExtrude","SWEPT_FACE",FACE,{"disambiguationData":[OSD([sQuery(id+"F4.wireOp",EDGE,"E30")])]}),makeQuery(id+"F8.opExtrude","SWEPT_FACE",FACE,{"disambiguationData":[OSD([sQuery(id+"F7.wireOp",EDGE,"E67")])]})]});
            fillet(context, id + "F14", {"entities" : qUnion([Q0, Q1, Q2, Q3, Q4, Q5]), "radius" : 3 * mm, "tangentPropagation" : true, "allowEdgeOverflow" : false});
        }
        {
            var Q0;
            Q0=makeQuery(id+"F1.opExtrude","CAP_EDGE",EDGE,{"disambiguationData":[OSD([sQuery(id+"F0.wireOp",EDGE,"E1.bottom")])],"isStart":false});
            fillet(context, id + "F15", {"entities" : qUnion([Q0]), "radius" : 2 * mm, "tangentPropagation" : true, "allowEdgeOverflow" : false});
        }
        {
            var Q0;
            Q0=qCreatedBy(makeId("Top.planeOp"),FACE);
            var sketch = newSketch(context, id + "F16", { "sketchPlane" : qUnion([Q0])});
            skArc(sketch, "E79.0.0", {"start": v(14.05, 38.38) * mm, "mid": v(16.98, 31.31) * mm, "end": v(24.05, 28.38) * mm});
            skLineSegment(sketch, "E79.0.1", {"start": v(24.05, 28.38) * mm, "end": v(164.05, 28.38) * mm});
            skArc(sketch, "E79.0.2", {"start": v(164.05, 28.38) * mm, "mid": v(171.12, 31.31) * mm, "end": v(174.05, 38.38) * mm});
            skLineSegment(sketch, "E79.0.3", {"start": v(174.05, 38.38) * mm, "end": v(174.05, 198.38) * mm});
            skArc(sketch, "E79.0.4", {"start": v(174.05, 198.38) * mm, "mid": v(171.12, 205.45) * mm, "end": v(164.05, 208.38) * mm});
            skLineSegment(sketch, "E79.0.5", {"start": v(164.05, 208.38) * mm, "end": v(24.05, 208.38) * mm});
            skArc(sketch, "E79.0.6", {"start": v(24.05, 208.38) * mm, "mid": v(16.98, 205.45) * mm, "end": v(14.05, 198.38) * mm});
            skLineSegment(sketch, "E79.0.7", {"start": v(14.05, 198.38) * mm, "end": v(14.05, 38.38) * mm});
            skLineSegment(sketch, "E80", {"start": v(127.05, 208.38) * mm, "end": v(109.05, 226.38) * mm});
            skLineSegment(sketch, "E81", {"start": v(109.05, 226.38) * mm, "end": v(109.05, 238.38) * mm});
            skLineSegment(sketch, "E82", {"start": v(61.05, 208.38) * mm, "end": v(79.05, 226.38) * mm});
            skLineSegment(sketch, "E83", {"start": v(79.05, 226.38) * mm, "end": v(79.05, 238.38) * mm});
            skArc(sketch, "E84", {"start": v(109.05, 238.38) * mm, "mid": v(94.05, 253.38) * mm, "end": v(79.05, 238.38) * mm});
            skLineSegment(sketch, "E85", {"start": v(94.05, 238.38) * mm, "end": v(94.05, 208.38) * mm, "construction": true});
            skCircle(sketch, "E86", {"center": v(94.05, 238.38) * mm, "radius": 6 * mm});
            skLineSegment(sketch, "E87", {"start": v(14.05, 118.38) * mm, "end": v(165.56, 118.38) * mm, "construction": true});
            skPoint(sketch, "E87.endSnap0", {"position": v(174.05, 118.38) * mm});
            skLineSegment(sketch, "E88.MirrorCS", {"start": v(164.05, 28.38) * mm, "end": v(24.05, 28.38) * mm});
            skLineSegment(sketch, "E89.MirrorCS", {"start": v(94.05, -1.62) * mm, "end": v(94.05, 28.38) * mm, "construction": true});
            skCircle(sketch, "E90.MirrorC", {"center": v(94.05, -1.62) * mm, "radius": 6 * mm});
            skLineSegment(sketch, "E91.MirrorCS", {"start": v(127.05, 28.38) * mm, "end": v(109.05, 10.38) * mm});
            skLineSegment(sketch, "E92.MirrorCS", {"start": v(109.05, 10.38) * mm, "end": v(109.05, -1.62) * mm});
            skLineSegment(sketch, "E93.MirrorCS", {"start": v(61.05, 28.38) * mm, "end": v(79.05, 10.38) * mm});
            skLineSegment(sketch, "E94.MirrorCS", {"start": v(79.05, 10.38) * mm, "end": v(79.05, -1.62) * mm});
            skArc(sketch, "E95.MirrorCS", {"start": v(109.05, -1.62) * mm, "mid": v(94.05, -16.62) * mm, "end": v(79.05, -1.62) * mm});
            skSolve(sketch);
        }
        {
            var Q0;
            {var subQ2=sQuery(id+"F16.wireOp",EDGE,"E80");Q0=makeQuery(id+"F16.imprint","IMPRINT",FACE,{"disambiguationData":[TD([[makeQuery(id+"F16.imprint","IMPRINT",EDGE,{"derivedFrom":subQ2}),1.0]])]});}
            var Q1;
            Q1=makeQuery(id+"F16.imprint","IMPRINT",FACE,{"disambiguationData":[TD([[makeQuery(id+"F16.imprint","IMPRINT",EDGE,{"derivedFrom":sQuery(id+"F16.wireOp",EDGE,"E90.MirrorC")}),1.0]])]});
            var Q2;
            Q2=makeQuery(id+"F2.opExtrude","CAP_FACE",FACE,{"disambiguationData":[OSD([sQuery(id+"F0.wireOp",EDGE,"E12"),sQuery(id+"F0.wireOp",EDGE,"E13"),sQuery(id+"F0.wireOp",EDGE,"E14"),sQuery(id+"F0.wireOp",EDGE,"E15"),sQuery(id+"F0.wireOp",EDGE,"E17.filletArc"),sQuery(id+"F0.wireOp",EDGE,"E18.filletArc"),sQuery(id+"F0.wireOp",EDGE,"E19.filletArc"),sQuery(id+"F0.wireOp",EDGE,"E20.filletArc"),sQuery(id+"F0.wireOp",EDGE,"E25.0"),sQuery(id+"F0.wireOp",EDGE,"E25.1"),sQuery(id+"F0.wireOp",EDGE,"E25.2"),sQuery(id+"F0.wireOp",EDGE,"E25.3"),sQuery(id+"F0.wireOp",EDGE,"E25.4"),sQuery(id+"F0.wireOp",EDGE,"E25.5"),sQuery(id+"F0.wireOp",EDGE,"E25.6"),sQuery(id+"F0.wireOp",EDGE,"E25.7")])],"isStart":false});
            extrude(context, id + "F17", {"entities" : qUnion([Q0, Q1]), "endBound" : BoundingType.UP_TO_SURFACE, "endBoundEntityFace" : qUnion([Q2]), "depth" : 25 * mm});
        }
    });
